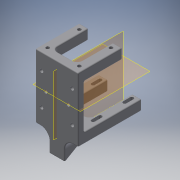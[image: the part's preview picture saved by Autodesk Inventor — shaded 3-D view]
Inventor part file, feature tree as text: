
AUTODESK INVENTOR PART (.ipt)
format: ipt  version: 2016 (Build 200138000, 138)  size: 528,384 bytes
history: native  units: mm
features: extrude x9, sketch x9, fillet x6, projected_geometry x6, plane x2, mirror x2, chamfer x1
ambient origin geometry x8: Origin, YZ Plane, XZ Plane, XY Plane, X Axis, Y Axis, Z Axis, Center Point
bodies: Solid1 (feature_tree)
feature tree (35):
  extrude  "Extrusion1"  Depth=43.0mm
  extrude  "Extrusion10"  Depth=10.0mm
  extrude  "Extrusion11"  Depth=42.0mm TaperAngle=0.0deg
  extrude  "Extrusion6"  Depth=3.3mm
  extrude  "Extrusion15"  Depth=31.0mm
  extrude  "Extrusion9"  Depth=31.0mm
  extrude  "Extrusion12"  Depth=22.0mm TaperAngle=0.0deg
  chamfer  "Chamfer1"  Distance=3.3mm
  plane  "Work Plane1"
  mirror  "Mirror2"
  extrude  "Extrusion13"  Depth=10.0mm
  fillet  "Fillet6"  Radius=3.3mm
  fillet  "Fillet7"  Radius=31.0mm
  fillet  "Fillet8"  Radius=3.3mm
  fillet  "Fillet5"  Radius=3.3mm
  extrude  "Extrusion14"  Depth=10.0mm
  fillet  "Fillet9"  Radius=3.3mm
  plane  "Work Plane2"
  mirror  "Mirror1"
  fillet  "Fillet10"  Radius=7.0mm
  sketch  "Sketch1"  dims[d0=43.0mm d1=43.0mm]
  sketch  "Sketch3"  dims[d2=10.0mm d3=6.0mm]
  sketch  "Sketch4"  dims[d4=62.0mm d5=42.0mm d6=0.0mm]
  projected_geometry  "Projected Loop4"
  sketch  "Sketch5"  dims[d15=3.3mm d16=3.3mm]
  sketch  "Sketch6"  dims[d17=6.5mm d18=31.0mm]
  projected_geometry  "Projected Loop6"
  projected_geometry  "Projected Loop7"
  projected_geometry  "Projected Loop8"
  sketch  "Sketch7"  dims[d19=3.3mm d20=31.0mm]
  projected_geometry  "Projected Loop9"
  sketch  "Sketch8"  dims[d21=3.3mm d28=22.0mm d29=0.0mm]
  sketch  "Sketch9"  dims[d36=3.3mm]
  sketch  "Sketch10"  dims[d37=20.0mm d38=3.3mm d39=3.3mm d41=3.3mm d42=31.0mm d43=3.3mm d44=3.3mm d45=3.3mm d46=3.3mm d47=7.0mm d48=31.0mm d49=42.0mm d50=0.0mm d51=9.0mm d52=9.0mm d53=24.0mm d54=42.0mm d55=0.0mm d56=9.0mm d57=9.0mm d58=35.0mm d59=0.0mm d63=3.5mm d64=3.5mm d65=3.5mm d66=3.5mm d67=3.5mm d69=6.0mm d70=6.0mm d71=42.0mm d72=0.0mm d74=10.0mm d75=60.0deg d76=10.0mm d77=15.0mm d78=0.0mm d79=5.0mm d80=17.0mm d81=9.0mm d82=6.0mm d83=0.8mm d84=5.0mm d85=15.0mm d86=0.0mm d87=1.0mm d88=1.0mm d89=2.0mm d90=2.0mm d91=45.0deg d92=31.0mm d96=12.0mm d97=0.0mm d98=3.5mm d99=10.0mm]
  projected_geometry  "Projected Loop10"
